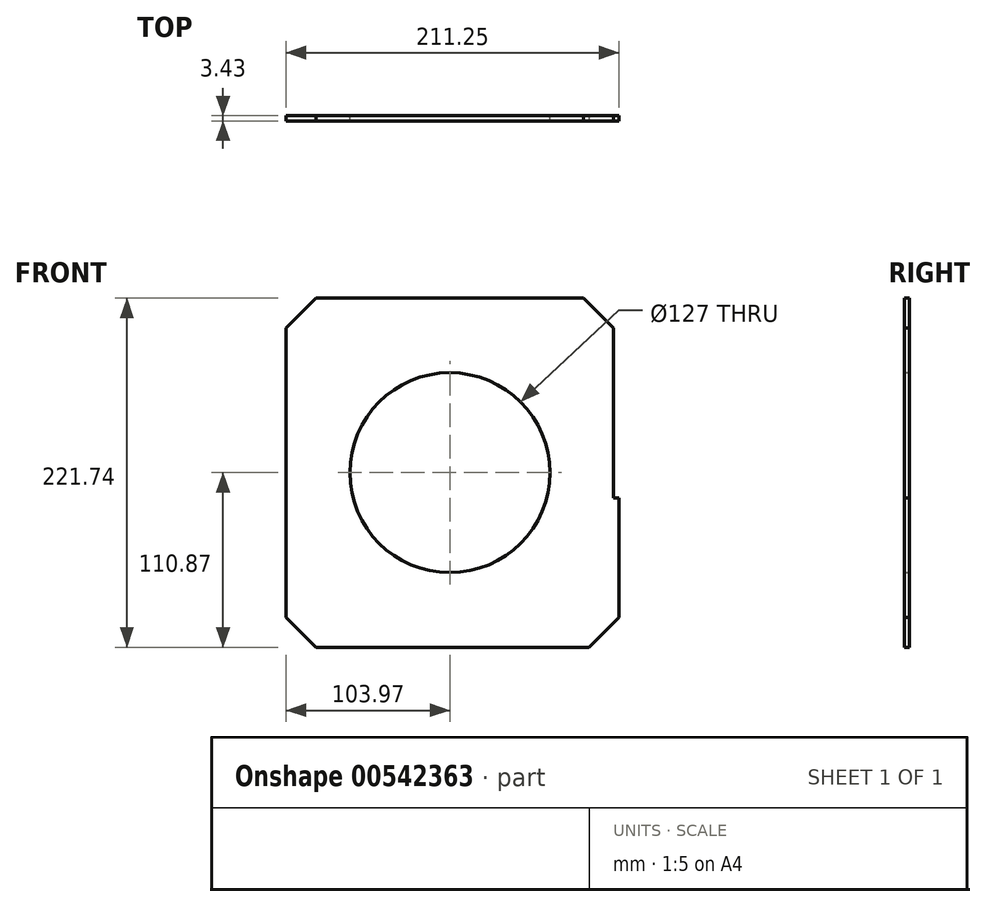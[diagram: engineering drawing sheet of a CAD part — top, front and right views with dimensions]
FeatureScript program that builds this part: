
annotation { "Feature Type Name" : "Feature", "Feature Type Description" : "" }
export const myFeature = defineFeature(function(context is Context, id is Id, definition is map)
    precondition{}
    {
        {
            var Q0;
            Q0=qCreatedBy(makeId("Front.planeOp"),FACE);
            var sketch = newSketch(context, id + "F0", { "sketchPlane" : qUnion([Q0])});
            skLineSegment(sketch, "E0.top", {"start": v(103.97, 110.87) * mm, "end": v(-103.97, 110.87) * mm});
            skLineSegment(sketch, "E0.right", {"start": v(-103.97, -110.87) * mm, "end": v(-103.97, 110.87) * mm});
            skPoint(sketch, "E0.middle", {"position": v(0, 0) * mm});
            skLineSegment(sketch, "E1.top", {"start": v(103.97, -16.13) * mm, "end": v(107.28, -16.13) * mm});
            skLineSegment(sketch, "E1.right", {"start": v(107.28, -110.87) * mm, "end": v(107.28, -16.13) * mm});
            skCircle(sketch, "E2", {"center": v(0, 0) * mm, "radius": 63.5 * mm});
            skLineSegment(sketch, "E3", {"start": v(103.97, 110.87) * mm, "end": v(103.97, -16.13) * mm});
            skLineSegment(sketch, "E4", {"start": v(107.28, -110.87) * mm, "end": v(-103.97, -110.87) * mm});
            skSolve(sketch);
        }
        {
            var Q0;
            Q0=makeQuery(id+"F0.imprint","IMPRINT",FACE,{"disambiguationData":[TD([[makeQuery(id+"F0.imprint","IMPRINT",EDGE,{"derivedFrom":sQuery(id+"F0.wireOp",EDGE,"E0.top")}),1.0]])]});
            extrude(context, id + "F1", {"entities" : qUnion([Q0]), "depth" : 3.43 * mm, "offsetDistance" : 25.4 * mm});
        }
        {
            var Q0;
            Q0=makeQuery(id+"F1.opExtrude","SWEPT_EDGE",EDGE,{"disambiguationData":[OSD([sQuery(id+"F0.wireOp",EDGE,"E0.top"),sQuery(id+"F0.wireOp",EDGE,"E0.right")])]});
            var Q1;
            Q1=makeQuery(id+"F1.opExtrude","SWEPT_EDGE",EDGE,{"disambiguationData":[OSD([sQuery(id+"F0.wireOp",EDGE,"E0.top"),sQuery(id+"F0.wireOp",EDGE,"E3")])]});
            var Q2;
            Q2=makeQuery(id+"F1.opExtrude","SWEPT_EDGE",EDGE,{"disambiguationData":[OSD([sQuery(id+"F0.wireOp",EDGE,"E1.right"),sQuery(id+"F0.wireOp",EDGE,"E4")])]});
            var Q3;
            Q3=makeQuery(id+"F1.opExtrude","SWEPT_EDGE",EDGE,{"disambiguationData":[OSD([sQuery(id+"F0.wireOp",EDGE,"E0.right"),sQuery(id+"F0.wireOp",EDGE,"E4")])]});
            chamfer(context, id + "F2", {"entities" : qUnion([Q0, Q1, Q2, Q3]), "width" : 19.05 * mm, "tangentPropagation" : true});
        }
    });
